# Revit family: DIVITYP017
name_source: partatom
category: Furniture
units: mm (PartAtom-declared; Revit-internal decimal feet)

## family parameters
Always vertical = Yes
Cut with Voids When Loaded = No
OmniClass Number = 23.40.20.00
OmniClass Title = General Furniture and Specialties
Render Appearance Source = Family Geometry
Room Calculation Point = No
Shared = No
Work Plane-Based = No

## types (1)
- DIVITYP017
    Cost = 85710 $
    Default Elevation = 0 mm  [stored 0 ft]
    Description = 6 x Upton - Black Mesh Back - Black Seat Fabric, 3 x BOX / FILE PEDESTAL MOBILE w/CUSHION 12"W, 3 x Box/File Mobile Ped-No Cushion-12W, 6 x Snap-In Data Plate w/6 Gang Face - Black, 3 x Black Duplex Outlet - Line 1, 3 x Black Duplex Outlet - Line 2, 3 x Black Duplex Outlet - Line 3, 3 x Black Duplex Outlet - Line 4 - Dedicated, 3 x 18 in. Electrical Jumper  (Panel To Panel), 3 x 21 in. Electrical Jumper  (Extended Panel To Panel), 1 x LH Receptacle Mounted Base Infeed - 72L - 8 Wire, 4 Circuit, 2 x DiVi LINEAR BASE RACEWAY SHROUD 3-WAY 90 DEGREES, 7 x DiVi LINEAR HARD PANEL-PWR-PERM MONO- 42H X 36W, 15 x DiVi LINEAR HARD PANEL -NPWR-PERMANENT MONOLITHIC- 42H X 36W, 8 x DIVI LINEAR BASE RACEWAY SHROUD END OF RUN, 6 x DiVi LINEAR STACK FRAME PANEL-FABRIC 24H X 36W MONO, 16 x DiVi LINEAR STACK FRAME GLASS PANEL-24H X 36W INSERT & MONO, 3 x WESKO FILE BAR - 12", 6 x TBL, REC, 2MM, 30DX72WX29H, HAL, E SERIES GLD 2 STAGE
    Exported From CET Designer = Yes
    Manufacturer = AIS
    Model = 4700
    Show DIVITYP017 = Yes
    VisibilityIndex = 0

note: [stored X ft] marks values corroborated as IEEE doubles in the binary element streams (Revit-internal decimal feet)

## geometry (parser evidence)
native form markers: Sweep x2
no freeform markers — native parametric forms only
